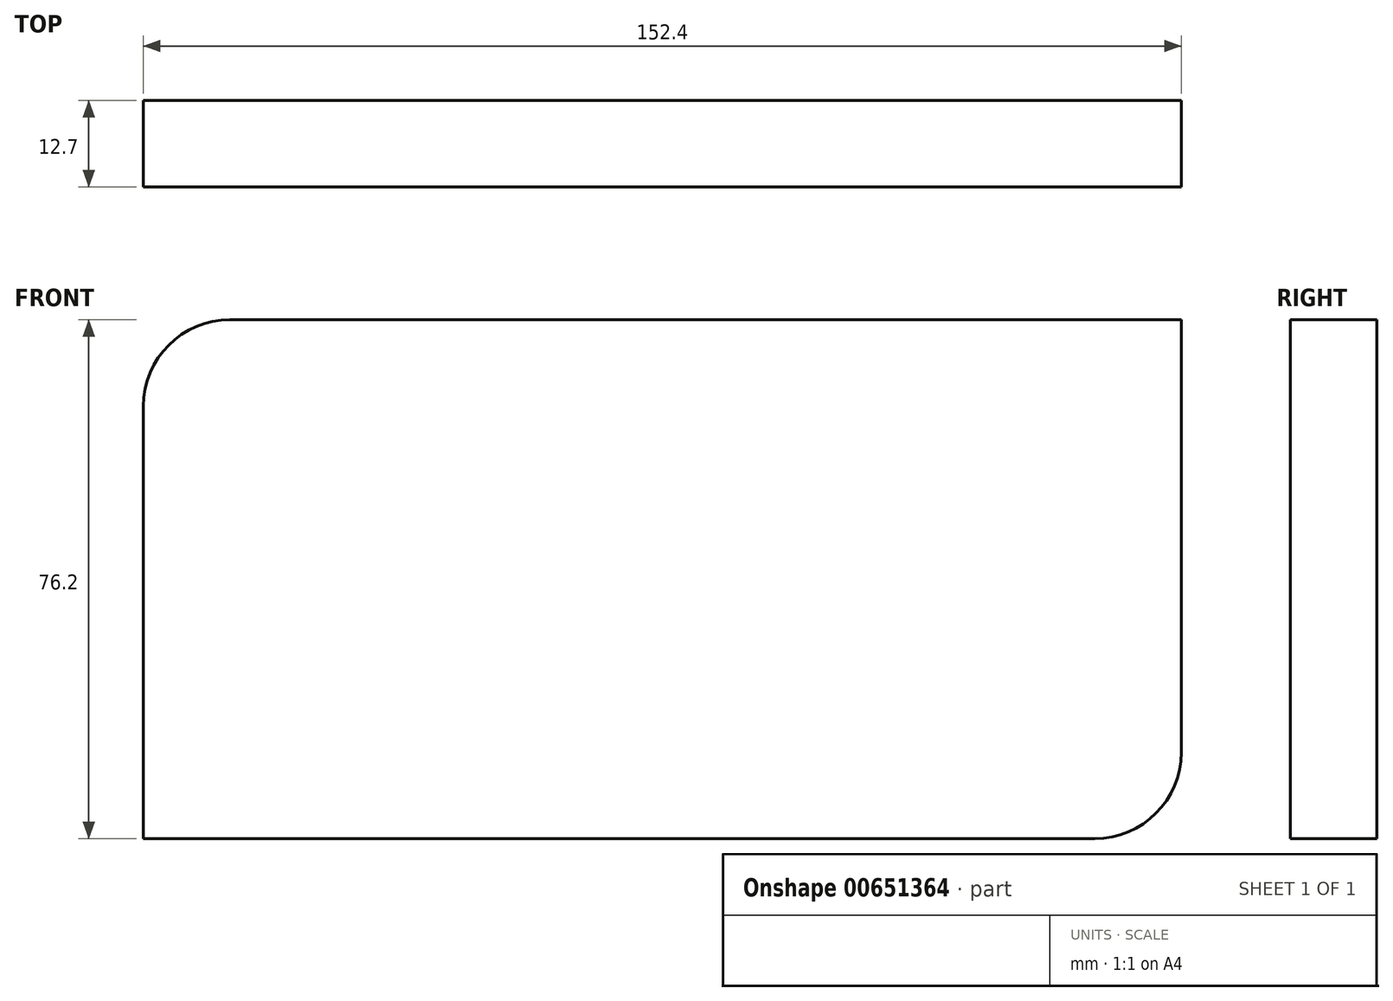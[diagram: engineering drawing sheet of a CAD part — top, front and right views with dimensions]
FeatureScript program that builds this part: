
annotation { "Feature Type Name" : "Feature", "Feature Type Description" : "" }
export const myFeature = defineFeature(function(context is Context, id is Id, definition is map)
    precondition{}
    {
        {
            var Q0;
            Q0=qCreatedBy(makeId("Front.planeOp"),FACE);
            var sketch = newSketch(context, id + "F0", { "sketchPlane" : qUnion([Q0])});
            skLineSegment(sketch, "E0.bottom", {"start": v(76.2, 38.1) * mm, "end": v(-63.5, 38.1) * mm});
            skLineSegment(sketch, "E0.top", {"start": v(63.5, -38.1) * mm, "end": v(-76.2, -38.1) * mm});
            skLineSegment(sketch, "E0.left", {"start": v(76.2, 38.1) * mm, "end": v(76.2, -25.4) * mm});
            skLineSegment(sketch, "E0.right", {"start": v(-76.2, 25.4) * mm, "end": v(-76.2, -38.1) * mm});
            skPoint(sketch, "E0.middle", {"position": v(0, 0) * mm});
            skPoint(sketch, "E1.visualSharp", {"position": v(-76.2, 38.1) * mm});
            skArc(sketch, "E1.filletArc", {"start": v(-63.5, 38.1) * mm, "mid": v(-72.48, 34.38) * mm, "end": v(-76.2, 25.4) * mm});
            skPoint(sketch, "E2.visualSharp", {"position": v(76.2, -38.1) * mm});
            skArc(sketch, "E2.filletArc", {"start": v(63.5, -38.1) * mm, "mid": v(72.48, -34.38) * mm, "end": v(76.2, -25.4) * mm});
            skSolve(sketch);
        }
        {
            var Q0;
            Q0=makeQuery(id+"F0.imprint","IMPRINT",FACE,{"disambiguationData":[TD([[makeQuery(id+"F0.imprint","IMPRINT",EDGE,{"derivedFrom":sQuery(id+"F0.wireOp",EDGE,"E0.bottom")}),1.0]])]});
            extrude(context, id + "F1", {"entities" : qUnion([Q0]), "depth" : 12.7 * mm, "offsetDistance" : 25.4 * mm});
        }
    });
